# Revit family: RHTG9030
name_source: partatom
category: Windows
units: mm (PartAtom-declared; Revit-internal decimal feet)

## family parameters
Always vertical = No
Cut with Voids When Loaded = No
Host = Roof
Room Calculation Point = No
Shared = No

## types (4) — shared parameters
Analytic Construction = <None>
Assembly Code = 37.22.28
Belastbaarheid = 250 kg/m²
Bestendigheid tegen sneeuwbelasting = 250 kg/m²
Bestendigheid tegen windbelasting = 3000 Pa
Dagkant = 82 mm  [stored 0.269029 ft]
Geluidwerendheid = 27 dB
Hard body impact test (EN 356) = Class P2A
Hatch Material = Gorter_Material 1
Isolatiewaarde HR+++ glas = Rc = 2,00 (m2.K)W; U = 0,50 W/(m2.K)
Isolatiewaarde opstand = Rc = 4,41 (m2.K)W; U = 0,227 W/(m2.K)
Luchtdichtheid = 0,5 m3/hm1
Manufacturer = Gorter
Model = RHTG
Oppervlaktebehandeling binnenzijde = Gepoedercoat RAL9010
Gepoedercoat in RAL7011 (buitenzijde) en RAL9010 (binnenzijde).
Gepoedercoat RAL 9010
Oppervlaktebehandeling buitenzijde = Gepoedercoat RAL9005 / RAL9010
Gepoedercoat in RAL7011 (buitenzijde) en RAL9010 (binnenzijde).
Gepoedercoat RAL 7011
Soft body impact test (EN 13049) = Class 5
URL = http://www.gortergroup.com
Wind- en waterdichtheid = 650 Pa

## per-type parameters (varying)
| type | A | A+136 | B | Height | Rough Height | Rough Width | Weight (kg) | Width |
| RHTG1015 | 1000 mm  [stored 3.28084 ft] | 1236 mm  [stored 4.05512 ft] | 1500 mm  [stored 4.92126 ft] | 1500 mm  [stored 4.92126 ft] | 1500 mm  [stored 4.92126 ft] | 1000 mm  [stored 3.28084 ft] | 221 | 1000 mm  [stored 3.28084 ft] |
| RHTG9024 | 900 mm  [stored 2.95276 ft] | 1136 mm  [stored 3.72703 ft] | 2400 mm | 2400 mm | 2400 mm | 900 mm  [stored 2.95276 ft] | 221 | 900 mm  [stored 2.95276 ft] |
| RHTG9030 | 900 mm  [stored 2.95276 ft] | 1136 mm  [stored 3.72703 ft] | 3000 mm  [stored 9.84252 ft] | 3000 mm  [stored 9.84252 ft] | 3000 mm  [stored 9.84252 ft] | 900 mm  [stored 2.95276 ft] | 268 | 900 mm  [stored 2.95276 ft] |
| RHTG1020 | 1000 mm  [stored 3.28084 ft] | 1236 mm  [stored 4.05512 ft] | 2000 mm  [stored 6.56168 ft] | 2000 mm  [stored 6.56168 ft] | 2000 mm  [stored 6.56168 ft] | 1000 mm  [stored 3.28084 ft] | 221 | 1000 mm  [stored 3.28084 ft] |

note: [stored X ft] marks values corroborated as IEEE doubles in the binary element streams (Revit-internal decimal feet)

## geometry (parser evidence)
native form markers: Sweep x2
no freeform markers — native parametric forms only
